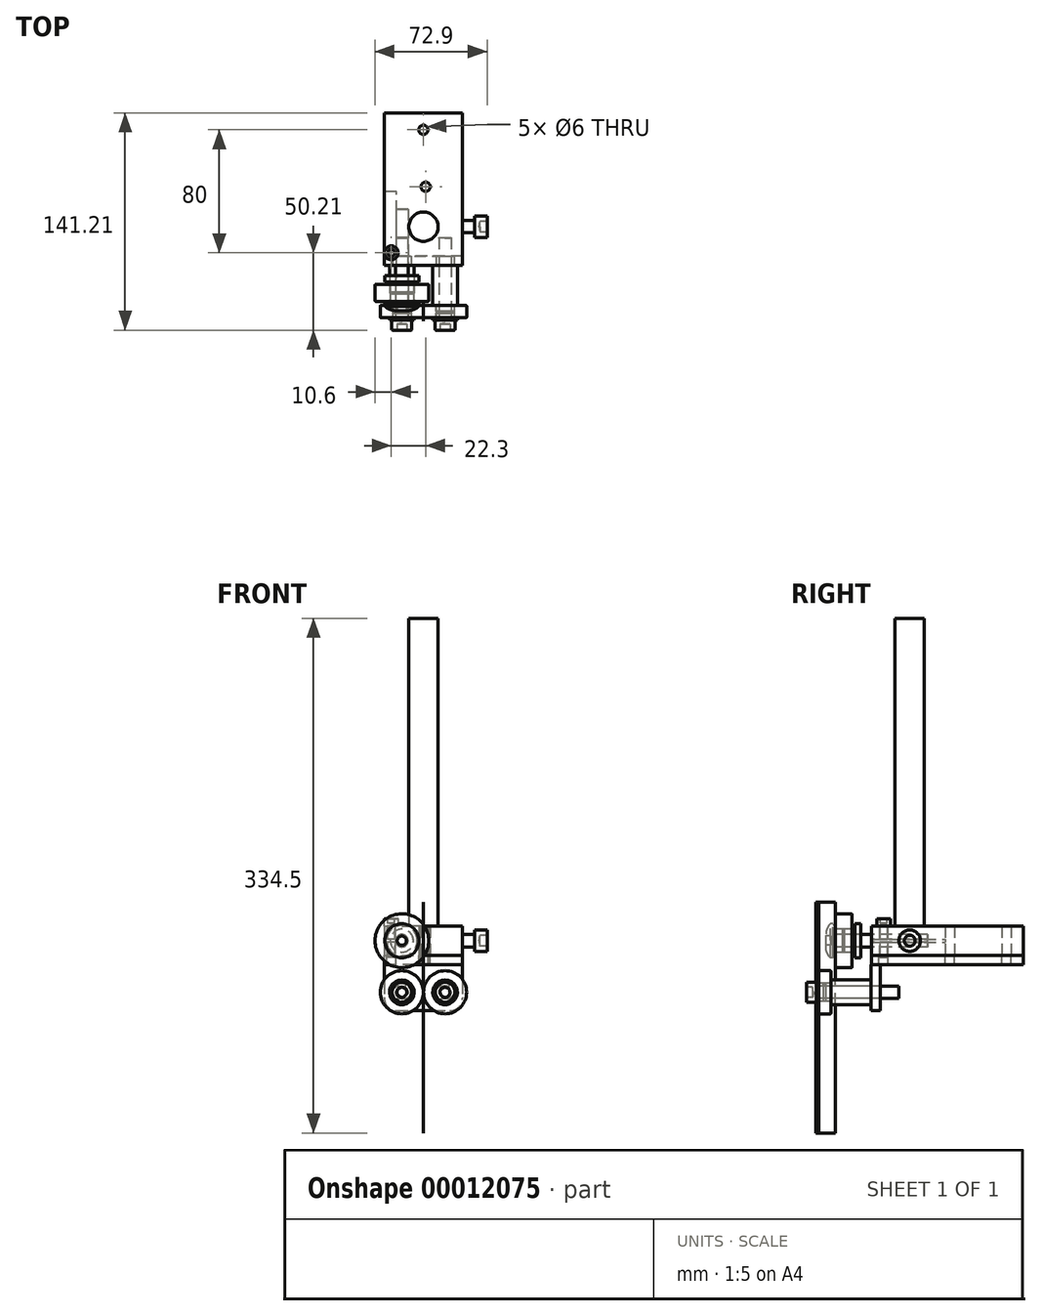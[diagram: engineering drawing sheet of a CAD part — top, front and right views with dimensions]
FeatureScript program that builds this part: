
annotation { "Feature Type Name" : "Feature", "Feature Type Description" : "" }
export const myFeature = defineFeature(function(context is Context, id is Id, definition is map)
    precondition{}
    {
        {
            var Q0;
            Q0=qCreatedBy(makeId("Top.planeOp"),FACE);
            var sketch = newSketch(context, id + "F0", { "sketchPlane" : qUnion([Q0])});
            skLineSegment(sketch, "E0.bottom", {"start": v(-25.4, 36.2) * mm, "end": v(25.4, 36.2) * mm});
            skLineSegment(sketch, "E0.top", {"start": v(-25.4, 135.2) * mm, "end": v(25.4, 135.2) * mm});
            skLineSegment(sketch, "E0.left", {"start": v(-25.4, 36.2) * mm, "end": v(-25.4, 135.2) * mm});
            skLineSegment(sketch, "E0.right", {"start": v(25.4, 36.2) * mm, "end": v(25.4, 135.2) * mm});
            skLineSegment(sketch, "E1", {"start": v(0, 93.09) * mm, "end": v(0, 23.02) * mm, "construction": true});
            skCircle(sketch, "E2", {"center": v(0, 124.2) * mm, "radius": 3 * mm});
            skCircle(sketch, "E3", {"center": v(1.4, 87.2) * mm, "radius": 3 * mm});
            skCircle(sketch, "E4", {"center": v(-20.9, 44.2) * mm, "radius": 2.5 * mm});
            skSolve(sketch);
        }
        {
            var Q0;
            Q0=qCreatedBy(makeId("Top.planeOp"),FACE);
            var sketch = newSketch(context, id + "F1", { "sketchPlane" : qUnion([Q0])});
            skLineSegment(sketch, "E5", {"start": v(-0.05, 12.7) * mm, "end": v(0.05, 12.7) * mm});
            skLineSegment(sketch, "E6", {"start": v(0.1, 0) * mm, "end": v(0.05, 2) * mm});
            skLineSegment(sketch, "E7", {"start": v(-0.1, 0) * mm, "end": v(-0.05, 2) * mm});
            skLineSegment(sketch, "E8", {"start": v(0, 0) * mm, "end": v(-0.1, 0) * mm});
            skLineSegment(sketch, "E9", {"start": v(0, 0) * mm, "end": v(0.1, 0) * mm});
            skLineSegment(sketch, "E10.trimOffspring", {"start": v(0.05, 2) * mm, "end": v(0.05, 12.7) * mm});
            skLineSegment(sketch, "E11.trimOffspring", {"start": v(-0.05, 2) * mm, "end": v(-0.05, 12.7) * mm});
            skPoint(sketch, "E12.orphan", {"position": v(0.1, 0) * mm});
            skPoint(sketch, "E13.orphan", {"position": v(-0.1, 0) * mm});
            skSolve(sketch);
        }
        {
            var Q0;
            Q0 = qSketchRegion(id + "F1", true);
            extrude(context, id + "F2", {"entities" : qUnion([Q0]), "oppositeDirection" : true, "depth" : 125 * mm, "hasSecondDirection" : true, "secondDirectionOppositeDirection" : false, "secondDirectionDepth" : 25 * mm});
        }
        {
            var Q0;
            Q0=makeQuery(id+"F0.imprint","IMPRINT",FACE,{"disambiguationData":[TD([[makeQuery(id+"F0.imprint","IMPRINT",EDGE,{"derivedFrom":sQuery(id+"F0.wireOp",EDGE,"E0.bottom")}),1.0]])]});
            extrude(context, id + "F3", {"entities" : qUnion([Q0]), "depth" : 19 * mm, "symmetric" : true});
        }
        {
            var Q0;
            Q0=qCreatedBy(makeId("Top.planeOp"),FACE);
            var sketch = newSketch(context, id + "F4", { "sketchPlane" : qUnion([Q0])});
            skLineSegment(sketch, "E14", {"start": v(41.4, 61.2) * mm, "end": v(48.28, 61.2) * mm, "construction": true});
            skLineSegment(sketch, "E15.0", {"start": v(25.4, 61.2) * mm, "end": v(25.4, 65.2) * mm});
            skLineSegment(sketch, "E16", {"start": v(25.4, 65.2) * mm, "end": v(33.4, 65.2) * mm});
            skPoint(sketch, "E17.orphan", {"position": v(25.4, 135.2) * mm});
            skPoint(sketch, "E18.orphan", {"position": v(25.4, 36.2) * mm});
            skLineSegment(sketch, "E19", {"start": v(33.4, 68.2) * mm, "end": v(33.4, 65.2) * mm});
            skLineSegment(sketch, "E20", {"start": v(33.4, 68.2) * mm, "end": v(41.4, 68.2) * mm});
            skLineSegment(sketch, "E21", {"start": v(41.4, 68.2) * mm, "end": v(41.4, 64.7) * mm});
            skLineSegment(sketch, "E22", {"start": v(25.4, 61.2) * mm, "end": v(36.05, 61.2) * mm});
            skLineSegment(sketch, "E23", {"start": v(41.4, 64.7) * mm, "end": v(36.66, 64.7) * mm});
            skLineSegment(sketch, "E24", {"start": v(36.66, 64.7) * mm, "end": v(36.05, 61.2) * mm});
            skSolve(sketch);
        }
        {
            var Q0;
            Q0 = qSketchRegion(id + "F4", true);
            var Q1;
            Q1=sQuery(id+"F4.wireOp",EDGE,"E14");
            revolve(context, id + "F5", {"operationType" : NewBodyOperationType.ADD, "entities" : qUnion([Q0]), "axis" : qUnion([Q1]), "revolveType" : RevolveType.FULL});
        }
        {
            var Q0;
            Q0=makeQuery(id+"F3.opExtrude","CAP_FACE",FACE,{"disambiguationData":[OSD([sQuery(id+"F0.wireOp",EDGE,"E0.bottom"),sQuery(id+"F0.wireOp",EDGE,"E0.top"),sQuery(id+"F0.wireOp",EDGE,"E0.left"),sQuery(id+"F0.wireOp",EDGE,"E0.right"),sQuery(id+"F0.wireOp",EDGE,"E2"),sQuery(id+"F0.wireOp",EDGE,"E3")])],"isStart":false});
            var sketch = newSketch(context, id + "F6", { "sketchPlane" : qUnion([Q0])});
            skCircle(sketch, "E25", {"center": v(0, 61.2) * mm, "radius": 9.53 * mm});
            skSolve(sketch);
        }
        {
            var Q0;
            Q0 = qSketchRegion(id + "F6", true);
            extrude(context, id + "F7", {"entities" : qUnion([Q0]), "operationType" : NewBodyOperationType.ADD, "depth" : 200 * mm});
        }
        {
            var Q0;
            Q0=makeQuery(id+"F2.opExtrude","SWEPT_FACE",FACE,{"disambiguationData":[OSD([sQuery(id+"F1.wireOp",EDGE,"E5")])]});
            cPlane(context, id + "F8", {"entities" : qUnion([Q0]), "cplaneType" : CPlaneType.OFFSET, "offset" : 0 * mm, "width" : 150 * mm, "height" : 150 * mm});
        }
        {
            var Q0;
            Q0=qCreatedBy(id+"F8.planeOp",FACE);
            var sketch = newSketch(context, id + "F9", { "sketchPlane" : qUnion([Q0])});
            skCircle(sketch, "E26", {"center": v(14, 0) * mm, "radius": 17.5 * mm});
            skCircle(sketch, "E27", {"center": v(14, 0) * mm, "radius": 7.5 * mm});
            skSolve(sketch);
        }
        {
            var Q0;
            Q0 = qSketchRegion(id + "F9", true);
            extrude(context, id + "F10", {"entities" : qUnion([Q0]), "operationType" : NewBodyOperationType.ADD, "depth" : 11 * mm});
        }
        {
            var Q0;
            Q0=makeQuery(id+"F2.opExtrude","SWEPT_FACE",FACE,{"disambiguationData":[OSD([sQuery(id+"F1.wireOp",EDGE,"E11.trimOffspring")])]});
            cPlane(context, id + "F11", {"entities" : qUnion([Q0]), "cplaneType" : CPlaneType.OFFSET, "offset" : 14 * mm, "width" : 150 * mm, "height" : 150 * mm});
        }
        {
            var Q0;
            Q0=qCreatedBy(id+"F11.planeOp",FACE);
            var sketch = newSketch(context, id + "F12", { "sketchPlane" : qUnion([Q0])});
            skPoint(sketch, "E28.orphan", {"position": v(-12.7, 25) * mm});
            skLineSegment(sketch, "E29.trimOffspring", {"start": v(-12.7, 4) * mm, "end": v(-72.7, 4) * mm});
            skLineSegment(sketch, "E30", {"start": v(-72.7, 4) * mm, "end": v(-72.7, 0) * mm});
            skLineSegment(sketch, "E31", {"start": v(-6.65, 3) * mm, "end": v(-9.98, 3) * mm});
            skLineSegment(sketch, "E32", {"start": v(-9.98, 3) * mm, "end": v(-9.98, 0) * mm});
            skPoint(sketch, "E33.visualSharp", {"position": v(-10.17, 11.27) * mm});
            skLineSegment(sketch, "E34", {"start": v(-9.98, 0) * mm, "end": v(-72.7, 0) * mm});
            skLineSegment(sketch, "E35", {"start": v(-23.7, 7.5) * mm, "end": v(-18.7, 7.5) * mm});
            skLineSegment(sketch, "E36.0", {"start": v(-11.2, 4.05) * mm, "end": v(-17.52, 4.05) * mm});
            skLineSegment(sketch, "E37", {"start": v(-25.31, 10) * mm, "end": v(-25.31, 4.05) * mm});
            skLineSegment(sketch, "E38", {"start": v(-25.31, 10) * mm, "end": v(-11.2, 10) * mm});
            skLineSegment(sketch, "E39", {"start": v(-11.2, 10) * mm, "end": v(-11.2, 4.05) * mm});
            skPoint(sketch, "E40.orphan", {"position": v(-10.66, 10) * mm});
            skPoint(sketch, "E41.orphan", {"position": v(-23.7, 17.5) * mm});
            skLineSegment(sketch, "E42.trimOffspring", {"start": v(-23.7, 7.5) * mm, "end": v(-23.7, 10) * mm});
            skLineSegment(sketch, "E43.trimOffspring", {"start": v(-23.7, 4) * mm, "end": v(-23.7, 4.05) * mm});
            skPoint(sketch, "E44.0.start.orphan", {"position": v(-23.7, -17.5) * mm});
            skPoint(sketch, "E45.orphan", {"position": v(-12.7, 17.5) * mm});
            skLineSegment(sketch, "E46.trimOffspring", {"start": v(-12.7, 7.5) * mm, "end": v(-12.7, 10) * mm});
            skPoint(sketch, "E47.0.start.orphan", {"position": v(-12.7, -17.5) * mm});
            skLineSegment(sketch, "E48", {"start": v(-18.7, 7.5) * mm, "end": v(-18.7, 4.05) * mm});
            skLineSegment(sketch, "E49", {"start": v(-17.52, 7.5) * mm, "end": v(-17.52, 4.05) * mm});
            skLineSegment(sketch, "E50.trimOffspring", {"start": v(-17.52, 7.5) * mm, "end": v(-12.7, 7.5) * mm});
            skLineSegment(sketch, "E51.trimOffspring", {"start": v(-18.7, 4.05) * mm, "end": v(-25.31, 4.05) * mm});
            skLineSegment(sketch, "E52", {"start": v(-12.7, 4) * mm, "end": v(-11.15, 4) * mm});
            skLineSegment(sketch, "E53.0", {"start": v(-11.15, 11.1) * mm, "end": v(-11.15, 4) * mm});
            skLineSegment(sketch, "E54", {"start": v(-11.15, 11.1) * mm, "end": v(-9.55, 11.1) * mm});
            skLineSegment(sketch, "E55.0", {"start": v(-6.65, 4) * mm, "end": v(-6.65, 3) * mm});
            skArc(sketch, "E56", {"start": v(-6.65, 4) * mm, "mid": v(-7.4, 7.83) * mm, "end": v(-9.55, 11.1) * mm});
            skLineSegment(sketch, "E57.0", {"start": v(-25.36, 11.15) * mm, "end": v(-25.36, 4.05) * mm});
            skLineSegment(sketch, "E58", {"start": v(-25.36, 4.05) * mm, "end": v(-29.36, 4.05) * mm});
            skLineSegment(sketch, "E59", {"start": v(-29.36, 4.05) * mm, "end": v(-29.36, 11.15) * mm});
            skLineSegment(sketch, "E60", {"start": v(-29.36, 11.15) * mm, "end": v(-25.36, 11.15) * mm});
            skSolve(sketch);
        }
        {
            var Q0;
            Q0 = qSketchRegion(id + "F12", true);
            var Q1;
            Q1=sQuery(id+"F12.wireOp",EDGE,"E34");
            revolve(context, id + "F13", {"entities" : qUnion([Q0]), "axis" : qUnion([Q1]), "revolveType" : RevolveType.FULL});
        }
        {
            var Q0;
            Q0=makeQuery(id+"F3.opExtrude","SWEPT_FACE",FACE,{"disambiguationData":[OSD([sQuery(id+"F0.wireOp",EDGE,"E0.left")])]});
            var sketch = newSketch(context, id + "F14", { "sketchPlane" : qUnion([Q0])});
            skLineSegment(sketch, "E61.0", {"start": v(-36.2, 1) * mm, "end": v(-84.16, 1) * mm});
            skLineSegment(sketch, "E62.0", {"start": v(-36.2, -1) * mm, "end": v(-84.16, -1) * mm});
            skLineSegment(sketch, "E63", {"start": v(-84.16, 1) * mm, "end": v(-84.16, -1) * mm});
            skLineSegment(sketch, "E64", {"start": v(-36.2, 1) * mm, "end": v(-36.2, -1) * mm});
            skSolve(sketch);
        }
        {
            var Q0;
            Q0 = qSketchRegion(id + "F14", true);
            var Q1;
            Q1=sQuery(id+"F14.wireOp",EDGE,"E61.0");
            var Q2;
            Q2=sQuery(id+"F14.wireOp",EDGE,"E62.0");
            extrude(context, id + "F15", {"entities" : qUnion([Q0]), "operationType" : NewBodyOperationType.REMOVE, "surfaceEntities" : qUnion([Q1, Q2]), "oppositeDirection" : true, "depth" : 8 * mm});
        }
        {
            var Q0;
            Q0=makeQuery(id+"F3.opExtrude","SWEPT_FACE",FACE,{"disambiguationData":[OSD([sQuery(id+"F0.wireOp",EDGE,"E0.left")])]});
            cPlane(context, id + "F16", {"entities" : qUnion([Q0]), "cplaneType" : CPlaneType.OFFSET, "offset" : 4.5 * mm, "oppositeDirection" : true, "width" : 150 * mm, "height" : 150 * mm});
        }
        {
            var Q0;
            Q0=qCreatedBy(id+"F16.planeOp",FACE);
            var sketch = newSketch(context, id + "F17", { "sketchPlane" : qUnion([Q0])});
            skLineSegment(sketch, "E65", {"start": v(-44.2, 10.8) * mm, "end": v(-44.2, -10.83) * mm});
            skLineSegment(sketch, "E66", {"start": v(-46.45, 14.15) * mm, "end": v(-48.7, 14.15) * mm});
            skLineSegment(sketch, "E67", {"start": v(-48.7, 14.15) * mm, "end": v(-48.7, 9.5) * mm});
            skLineSegment(sketch, "E68", {"start": v(-46.7, 9.5) * mm, "end": v(-46.7, -10.83) * mm});
            skLineSegment(sketch, "E69", {"start": v(-44.2, -10.83) * mm, "end": v(-46.7, -10.83) * mm});
            skLineSegment(sketch, "E70.0", {"start": v(-46.7, 9.5) * mm, "end": v(-48.7, 9.5) * mm});
            skPoint(sketch, "E71.orphan", {"position": v(-36.2, 9.5) * mm});
            skPoint(sketch, "E72.orphan", {"position": v(-135.2, 9.5) * mm});
            skLineSegment(sketch, "E73", {"start": v(-46.45, 14.15) * mm, "end": v(-46.45, 11.38) * mm});
            skLineSegment(sketch, "E74", {"start": v(-46.45, 11.38) * mm, "end": v(-44.2, 10.8) * mm});
            skPoint(sketch, "E75.orphan", {"position": v(-44.2, 14.15) * mm});
            skSolve(sketch);
        }
        {
            var Q0;
            Q0 = qSketchRegion(id + "F17", true);
            var Q1;
            Q1=sQuery(id+"F17.wireOp",EDGE,"E65");
            revolve(context, id + "F18", {"entities" : qUnion([Q0]), "axis" : qUnion([Q1]), "revolveType" : RevolveType.FULL});
        }
        {
            var Q0;
            Q0=makeQuery(id+"F2.opExtrude","CAP_VERTEX",VERTEX,{"disambiguationData":[OSD([sQuery(id+"F1.wireOp",EDGE,"E6"),sQuery(id+"F1.wireOp",EDGE,"E10.trimOffspring")])],"isStart":true});
            var Q1;
            Q1=makeQuery(id+"F2.opExtrude","CAP_VERTEX",VERTEX,{"disambiguationData":[OSD([sQuery(id+"F1.wireOp",EDGE,"E7"),sQuery(id+"F1.wireOp",EDGE,"E11.trimOffspring")])],"isStart":true});
            var Q2;
            Q2=makeQuery(id+"F2.opExtrude","CAP_VERTEX",VERTEX,{"disambiguationData":[OSD([sQuery(id+"F1.wireOp",EDGE,"E7"),sQuery(id+"F1.wireOp",EDGE,"E11.trimOffspring")])],"isStart":false});
            cPlane(context, id + "F19", {"entities" : qUnion([Q0, Q1, Q2]), "cplaneType" : CPlaneType.THREE_POINT, "offset" : 0 * mm, "width" : 150 * mm, "height" : 150 * mm});
        }
        {
            var Q0;
            Q0=qCreatedBy(id+"F19.planeOp",FACE);
            var sketch = newSketch(context, id + "F20", { "sketchPlane" : qUnion([Q0])});
            skCircle(sketch, "E76", {"center": v(14.1, -33.5) * mm, "radius": 14 * mm});
            skCircle(sketch, "E77", {"center": v(14.1, -33.5) * mm, "radius": 6 * mm});
            skCircle(sketch, "E78", {"center": v(-14.1, -33.5) * mm, "radius": 14 * mm});
            skLineSegment(sketch, "E79", {"start": v(14.1, -33.5) * mm, "end": v(-14.1, -33.5) * mm, "construction": true});
            skCircle(sketch, "E80", {"center": v(-14.1, -33.5) * mm, "radius": 6 * mm});
            skLineSegment(sketch, "E81.0", {"start": v(0.1, -33.5) * mm, "end": v(0.1, -33.5) * mm});
            skPoint(sketch, "E82.orphan", {"position": v(0.1, -125) * mm});
            skPoint(sketch, "E83.orphan", {"position": v(0.1, 25) * mm});
            skSolve(sketch);
        }
        {
            var Q0;
            Q0 = qSketchRegion(id + "F20", true);
            extrude(context, id + "F21", {"entities" : qUnion([Q0]), "depth" : 8 * mm});
        }
        {
            var Q0;
            {var subQ0=sQuery(id+"F9.wireOp",EDGE,"E26");Q0=makeQuery(id+"F10.boolean.opBoolean","SPLIT",EDGE,{"disambiguationData":[TD([makeQuery(id+"F2.opExtrude","SWEPT_FACE",FACE,{"disambiguationData":[OSD([sQuery(id+"F1.wireOp",EDGE,"E5")])]}),makeQuery(id+"F2.opExtrude","SWEPT_FACE",FACE,{"disambiguationData":[OSD([sQuery(id+"F1.wireOp",EDGE,"E11.trimOffspring")])]}),makeQuery(id+"F10.opExtrude","SWEPT_FACE",FACE,{"disambiguationData":[OSD([subQ0])]}),makeQuery(id+"F10.opExtrude","CAP_FACE",FACE,{"disambiguationData":[OSD([subQ0,sQuery(id+"F9.wireOp",EDGE,"E27")])],"isStart":true})])],"derivedFrom":makeQuery(id+"F10.opExtrude","CAP_EDGE",EDGE,{"disambiguationData":[OSD([subQ0])],"isStart":true})});}
            var Q1;
            Q1=makeQuery(id+"F10.opExtrude","CAP_EDGE",EDGE,{"disambiguationData":[OSD([sQuery(id+"F9.wireOp",EDGE,"E26")])],"isStart":false});
            var Q2;
            Q2=makeQuery(id+"F21.opExtrude","CAP_EDGE",EDGE,{"disambiguationData":[OSD([sQuery(id+"F20.wireOp",EDGE,"E76")])],"isStart":true});
            var Q3;
            Q3=makeQuery(id+"F21.opExtrude","CAP_EDGE",EDGE,{"disambiguationData":[OSD([sQuery(id+"F20.wireOp",EDGE,"E76")])],"isStart":false});
            var Q4;
            Q4=makeQuery(id+"F21.opExtrude","CAP_EDGE",EDGE,{"disambiguationData":[OSD([sQuery(id+"F20.wireOp",EDGE,"E78")])],"isStart":false});
            var Q5;
            Q5=makeQuery(id+"F21.opExtrude","CAP_EDGE",EDGE,{"disambiguationData":[OSD([sQuery(id+"F20.wireOp",EDGE,"E78")])],"isStart":true});
            var Q6;
            {var subQ0=sQuery(id+"F9.wireOp",EDGE,"E26");Q6=makeQuery(id+"F10.boolean.opBoolean","SPLIT",EDGE,{"disambiguationData":[TD([makeQuery(id+"F2.opExtrude","SWEPT_FACE",FACE,{"disambiguationData":[OSD([sQuery(id+"F1.wireOp",EDGE,"E5")])]}),makeQuery(id+"F2.opExtrude","SWEPT_FACE",FACE,{"disambiguationData":[OSD([sQuery(id+"F1.wireOp",EDGE,"E10.trimOffspring")])]}),makeQuery(id+"F10.opExtrude","SWEPT_FACE",FACE,{"disambiguationData":[OSD([subQ0])]}),makeQuery(id+"F10.opExtrude","CAP_FACE",FACE,{"disambiguationData":[OSD([subQ0,sQuery(id+"F9.wireOp",EDGE,"E27")])],"isStart":true})])],"derivedFrom":makeQuery(id+"F10.opExtrude","CAP_EDGE",EDGE,{"disambiguationData":[OSD([subQ0])],"isStart":true})});}
            fillet(context, id + "F22", {"entities" : qUnion([Q0, Q1, Q2, Q3, Q4, Q5, Q6]), "radius" : .5 * mm, "tangentPropagation" : true, "allowEdgeOverflow" : false});
        }
        {
            var Q0;
            Q0=makeQuery(id+"F21.opExtrude","CAP_FACE",FACE,{"disambiguationData":[OSD([sQuery(id+"F20.wireOp",EDGE,"E78"),sQuery(id+"F20.wireOp",EDGE,"E80")])],"isStart":false});
            cPlane(context, id + "F23", {"entities" : qUnion([Q0]), "cplaneType" : CPlaneType.OFFSET, "offset" : 26 * mm, "width" : 150 * mm, "height" : 150 * mm});
        }
        {
            var Q0;
            Q0=qCreatedBy(id+"F23.planeOp",FACE);
            var sketch = newSketch(context, id + "F24", { "sketchPlane" : qUnion([Q0])});
            skLineSegment(sketch, "E84", {"start": v(37.24, -33.5) * mm, "end": v(-40.56, -33.5) * mm, "construction": true});
            skLineSegment(sketch, "E85.0", {"start": v(16.06, -29.5) * mm, "end": v(12.06, -29.5) * mm});
            skLineSegment(sketch, "E86.0", {"start": v(16.06, -37.5) * mm, "end": v(12.06, -37.5) * mm});
            skArc(sketch, "E87", {"start": v(-16.06, -29.5) * mm, "mid": v(-20.06, -33.5) * mm, "end": v(-16.06, -37.5) * mm});
            skLineSegment(sketch, "E88", {"start": v(0, -46.27) * mm, "end": v(0, -63.75) * mm, "construction": true});
            skArc(sketch, "E89.MirrorC", {"start": v(16.06, -29.5) * mm, "mid": v(20.06, -33.5) * mm, "end": v(16.06, -37.5) * mm});
            skArc(sketch, "E90", {"start": v(-12.06, -37.5) * mm, "mid": v(-8.06, -33.5) * mm, "end": v(-12.06, -29.5) * mm});
            skArc(sketch, "E91.MirrorC", {"start": v(12.06, -37.5) * mm, "mid": v(8.06, -33.5) * mm, "end": v(12.06, -29.5) * mm});
            skLineSegment(sketch, "E92.trimOffspring", {"start": v(-12.06, -37.5) * mm, "end": v(-16.06, -37.5) * mm});
            skLineSegment(sketch, "E93.trimOffspring", {"start": v(-12.06, -29.5) * mm, "end": v(-16.06, -29.5) * mm});
            skLineSegment(sketch, "E94", {"start": v(25.4, -15.5) * mm, "end": v(25.4, -37.5) * mm});
            skLineSegment(sketch, "E95", {"start": v(17.4, -45.5) * mm, "end": v(-17.4, -45.5) * mm});
            skLineSegment(sketch, "E96", {"start": v(-25.4, -15.5) * mm, "end": v(-25.4, -37.5) * mm});
            skPoint(sketch, "E97.visualSharp", {"position": v(25.4, -45.5) * mm});
            skArc(sketch, "E97.filletArc", {"start": v(17.4, -45.5) * mm, "mid": v(23.06, -43.16) * mm, "end": v(25.4, -37.5) * mm});
            skPoint(sketch, "E98.visualSharp", {"position": v(-25.4, -45.5) * mm});
            skArc(sketch, "E98.filletArc", {"start": v(-25.4, -37.5) * mm, "mid": v(-23.06, -43.16) * mm, "end": v(-17.4, -45.5) * mm});
            skLineSegment(sketch, "E99", {"start": v(-25.4, -15.5) * mm, "end": v(25.4, -15.5) * mm});
            skPoint(sketch, "E100.0.end.orphan", {"position": v(-25.4, -9.5) * mm});
            skPoint(sketch, "E101.orphan", {"position": v(25.4, -9.5) * mm});
            skSolve(sketch);
        }
        {
            var Q0;
            Q0=makeQuery(id+"F24.imprint","IMPRINT",FACE,{"disambiguationData":[TD([[makeQuery(id+"F24.imprint","IMPRINT",EDGE,{"derivedFrom":sQuery(id+"F24.wireOp",EDGE,"E85.0")}),-1.0]])]});
            extrude(context, id + "F25", {"entities" : qUnion([Q0]), "operationType" : NewBodyOperationType.ADD, "depth" : 6 * mm});
        }
        {
            var Q0;
            Q0=makeQuery(id+"F3.opExtrude","CAP_FACE",FACE,{"disambiguationData":[OSD([sQuery(id+"F0.wireOp",EDGE,"E0.bottom"),sQuery(id+"F0.wireOp",EDGE,"E0.top"),sQuery(id+"F0.wireOp",EDGE,"E0.left"),sQuery(id+"F0.wireOp",EDGE,"E0.right"),sQuery(id+"F0.wireOp",EDGE,"E2"),sQuery(id+"F0.wireOp",EDGE,"E3"),sQuery(id+"F0.wireOp",EDGE,"E4")])],"isStart":true});
            var sketch = newSketch(context, id + "F26", { "sketchPlane" : qUnion([Q0])});
            skLineSegment(sketch, "E102.0.0", {"start": v(-25.4, -36.2) * mm, "end": v(-25.4, -36.2) * mm});
            skLineSegment(sketch, "E102.0.1", {"start": v(-25.4, -135.2) * mm, "end": v(25.4, -135.2) * mm});
            skLineSegment(sketch, "E102.0.2", {"start": v(25.4, -135.2) * mm, "end": v(25.4, -36.2) * mm});
            skPoint(sketch, "E103.orphan", {"position": v(-25.4, -36.2) * mm});
            skLineSegment(sketch, "E104.0", {"start": v(-25.4, -36.2) * mm, "end": v(25.4, -36.2) * mm});
            skPoint(sketch, "E105.orphan", {"position": v(25.4, -36.2) * mm});
            skCircle(sketch, "E106.0", {"center": v(0, -124.2) * mm, "radius": 3 * mm});
            skCircle(sketch, "E106.1", {"center": v(1.4, -87.2) * mm, "radius": 3 * mm});
            skCircle(sketch, "E107", {"center": v(-20.9, -44.2) * mm, "radius": 3 * mm});
            skLineSegment(sketch, "E108", {"start": v(-25.4, -36.2) * mm, "end": v(-25.4, -135.2) * mm});
            skSolve(sketch);
        }
        {
            var Q0;
            Q0 = qSketchRegion(id + "F26", true);
            extrude(context, id + "F27", {"entities" : qUnion([Q0]), "depth" : 6 * mm});
        }
        {
            var Q0;
            Q0=qCreatedBy(id+"F11.planeOp",FACE);
            var sketch = newSketch(context, id + "F28", { "sketchPlane" : qUnion([Q0])});
            skLineSegment(sketch, "E109.0", {"start": v(-0.5, -25.5) * mm, "end": v(-2, -25.5) * mm});
            skLineSegment(sketch, "E110", {"start": v(-10, -27.5) * mm, "end": v(-6.35, -27.5) * mm});
            skLineSegment(sketch, "E111", {"start": v(-6.35, -27.5) * mm, "end": v(-6.35, -29.5) * mm});
            skLineSegment(sketch, "E112", {"start": v(-5.01, -27.5) * mm, "end": v(-5.01, -29.5) * mm});
            skLineSegment(sketch, "E113", {"start": v(-0.5, -25.5) * mm, "end": v(-0.5, -29.5) * mm});
            skLineSegment(sketch, "E114", {"start": v(-36, -29.5) * mm, "end": v(-6.35, -29.5) * mm});
            skLineSegment(sketch, "E115.trimOffspring", {"start": v(-10, -25.5) * mm, "end": v(-36, -25.5) * mm});
            skLineSegment(sketch, "E116.trimOffspring", {"start": v(-5.01, -27.5) * mm, "end": v(-2, -27.5) * mm});
            skLineSegment(sketch, "E117.trimOffspring", {"start": v(-5.01, -29.5) * mm, "end": v(-0.5, -29.5) * mm});
            skLineSegment(sketch, "E118.0", {"start": v(-0.45, -27) * mm, "end": v(-0.45, -29.55) * mm});
            skLineSegment(sketch, "E119", {"start": v(-0.45, -27) * mm, "end": v(6, -27) * mm});
            skLineSegment(sketch, "E120", {"start": v(6, -27) * mm, "end": v(6, -30.26) * mm});
            skLineSegment(sketch, "E121", {"start": v(-0.45, -29.55) * mm, "end": v(-54, -29.6) * mm});
            skLineSegment(sketch, "E122", {"start": v(-54, -29.6) * mm, "end": v(-54, -33.5) * mm});
            skLineSegment(sketch, "E123", {"start": v(6, -30.26) * mm, "end": v(1.99, -30.26) * mm});
            skLineSegment(sketch, "E124", {"start": v(1.99, -30.26) * mm, "end": v(1.39, -33.52) * mm});
            skLineSegment(sketch, "E125", {"start": v(-2, -25.5) * mm, "end": v(-2, -27.5) * mm});
            skLineSegment(sketch, "E126", {"start": v(-10, -25.5) * mm, "end": v(-10, -27.5) * mm});
            skLineSegment(sketch, "E127", {"start": v(-36, -25.5) * mm, "end": v(-36, -29.5) * mm});
            skLineSegment(sketch, "E128", {"start": v(-54, -33.5) * mm, "end": v(1.39, -33.52) * mm});
            skSolve(sketch);
        }
        {
            var Q0;
            Q0=makeQuery(id+"F28.imprint","IMPRINT",FACE,{"disambiguationData":[TD([[makeQuery(id+"F28.imprint","IMPRINT",EDGE,{"derivedFrom":sQuery(id+"F28.wireOp",EDGE,"E118.0")}),1.0]])]});
            var Q1;
            Q1=makeQuery(id+"F28.imprint","IMPRINT",FACE,{"disambiguationData":[TD([[makeQuery(id+"F28.imprint","IMPRINT",EDGE,{"derivedFrom":sQuery(id+"F28.wireOp",EDGE,"E109.0")}),1.0]])]});
            var Q2;
            Q2=makeQuery(id+"F28.imprint","IMPRINT",FACE,{"disambiguationData":[TD([[makeQuery(id+"F28.imprint","IMPRINT",EDGE,{"derivedFrom":sQuery(id+"F28.wireOp",EDGE,"E110")}),-1.0]])]});
            var Q3;
            Q3=sQuery(id+"F28.wireOp",EDGE,"E128");
            revolve(context, id + "F29", {"entities" : qUnion([Q0, Q1, Q2]), "axis" : qUnion([Q3]), "revolveType" : RevolveType.FULL});
        }
        {
            var Q0;
            Q0=makeQuery(id+"F29.opRevolve","SWEPT_BODY",BODY,{"disambiguationData":[OSD([sQuery(id+"F28.wireOp",EDGE,"aebac700-1d01-497d-9071-5db726c92a9f.0"),sQuery(id+"F28.wireOp",EDGE,"E110"),sQuery(id+"F28.wireOp",EDGE,"E111"),sQuery(id+"F28.wireOp",EDGE,"E114"),sQuery(id+"F28.wireOp",EDGE,"E115.trimOffspring"),sQuery(id+"F28.wireOp",EDGE,"0ac6e527-c36b-4fa0-a7a7-f8bd3b4da788.trimOffspring")])]});
            var Q1;
            Q1=makeQuery(id+"F29.opRevolve","SWEPT_BODY",BODY,{"disambiguationData":[OSD([sQuery(id+"F28.wireOp",EDGE,"E109.0"),sQuery(id+"F28.wireOp",EDGE,"E112"),sQuery(id+"F28.wireOp",EDGE,"0a931d74-9232-45cf-b0bc-34311335d83e.0"),sQuery(id+"F28.wireOp",EDGE,"E113"),sQuery(id+"F28.wireOp",EDGE,"E116.trimOffspring"),sQuery(id+"F28.wireOp",EDGE,"E117.trimOffspring")])]});
            var Q2;
            Q2=makeQuery(id+"F29.opRevolve","SWEPT_BODY",BODY,{"disambiguationData":[OSD([sQuery(id+"F28.wireOp",EDGE,"E118.0"),sQuery(id+"F28.wireOp",EDGE,"E119"),sQuery(id+"F28.wireOp",EDGE,"E120"),sQuery(id+"F28.wireOp",EDGE,"E121"),sQuery(id+"F28.wireOp",EDGE,"E122"),sQuery(id+"F28.wireOp",EDGE,"E123"),sQuery(id+"F28.wireOp",EDGE,"E124"),sQuery(id+"F28.wireOp",EDGE,"E128")])]});
            var Q3;
            Q3=qCreatedBy(makeId("Right.planeOp"),FACE);
            mirror(context, id + "F30", {"entities" : qUnion([Q0, Q1, Q2]), "mirrorPlane" : qUnion([Q3])});
        }
    });
